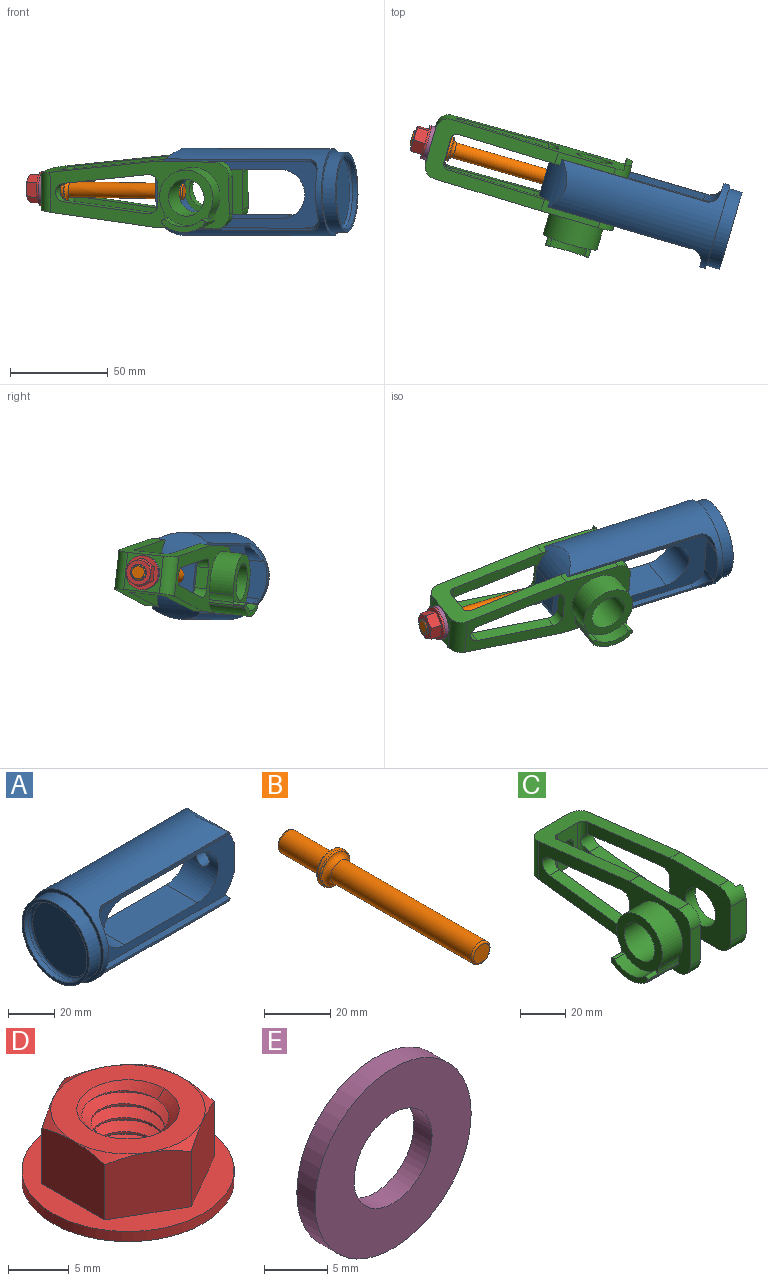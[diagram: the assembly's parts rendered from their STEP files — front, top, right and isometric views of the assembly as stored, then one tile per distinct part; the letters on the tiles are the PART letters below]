
ASSEMBLY  parts=5 mates=5
PART A: 35 faces, bbox 99.1x44.5x44.5 mm
  f0: cylinder r=22.23mm len=85.62mm, axis (-1,0,0), area 4765.1mm2, adj f4,f5,f8,f9,f12,f13,f22,f25
  f1: plane 88.9x34.29mm, normal (0,1,0), area 1346.2mm2, adj f3,f6,f7,f12,f14,f15,f16,f17
  f2: plane 88.9x34.29mm, normal (0,-1,0), area 1346.2mm2, adj f3,f10,f11,f13,f14,f15,f16,f17
  f3: plane 19.05x15.86mm, normal (1,0,0), area 252.7mm2, adj f1,f2,f24,f25,f26
  f4: plane 77.16x1.2mm, normal (0,1,0), area 83.9mm2, adj f0,f6,f19,f25,f29
  f5: plane 77.16x1.2mm, normal (0,1,0), area 83.9mm2, adj f0,f7,f20,f26,f30
  f6: plane 75.89x3.18mm, normal (0,0,-1), area 241mm2, adj f1,f4,f19,f25
  f7: plane 75.89x3.18mm, normal (0,0,1), area 241mm2, adj f1,f5,f20,f26
  f8: plane 77.16x1.2mm, normal (0,-1,0), area 83.9mm2, adj f0,f11,f18,f25,f27
  f9: plane 77.16x1.2mm, normal (0,-1,0), area 83.9mm2, adj f0,f10,f21,f26,f28
  f10: plane 75.89x3.18mm, normal (0,0,1), area 241mm2, adj f2,f9,f21,f26
  f11: plane 75.89x3.18mm, normal (0,0,-1), area 241mm2, adj f2,f8,f18,f25
  f12: plane 22.9x12.7mm, normal (1,0,0), area 230.7mm2, adj f0,f1,f19,f20,f29,f30
  f13: plane 22.9x12.7mm, normal (1,0,0), area 230.7mm2, adj f0,f2,f18,f21,f27,f28
  f14: plane 44.45x19.05mm, normal (0,0,-1), area 846.8mm2, adj f1,f2,f15,f17
  f15: cylinder r=12.7mm len=25.4mm, axis (0,-1,0), area 760.1mm2, adj f1,f2,f14,f16
  f16: plane 44.45x19.05mm, normal (0,0,1), area 846.8mm2, adj f1,f2,f15,f17
  f17: cylinder r=12.7mm len=25.4mm, axis (0,-1,0), area 709.9mm2, adj f1,f2,f14,f16,f24
  f18: cylinder r=7.62mm len=9.53mm, axis (0,-1,0), area 63.1mm2, adj f2,f8,f11,f13,f27
  f19: cylinder r=7.62mm len=9.53mm, axis (0,-1,0), area 63.1mm2, adj f1,f4,f6,f12,f29
  f20: cylinder r=7.62mm len=9.53mm, axis (0,1,0), area 63.1mm2, adj f1,f5,f7,f12,f30
  f21: cylinder r=7.62mm len=9.53mm, axis (0,1,0), area 63.1mm2, adj f2,f9,f10,f13,f28
  f22: plane 44.45x44.45mm, normal (-1,0,0), area 230.2mm2, adj f0,f23
  f23: cylinder r=20.51mm len=41.02mm, axis (-1,0,0), area 900.2mm2, adj f22,f32
  f24: cylinder r=3.97mm len=10.16mm, axis (1,0,0), area 245.4mm2, adj f3,f17
  f25: cylinder r=25.4mm len=25.4mm, axis (0,-1,0), area 355.4mm2, adj f0,f1,f2,f3,f4,f6,f8,f11
  f26: cylinder r=25.4mm len=25.4mm, axis (0,-1,0), area 355.4mm2, adj f0,f1,f2,f3,f5,f7,f9,f10
  f27: cylinder r=6.35mm len=8.71mm, axis (0,0,1), area 20.6mm2, adj f0,f8,f13,f18
  f28: cylinder r=6.35mm len=8.71mm, axis (0,0,1), area 20.6mm2, adj f0,f9,f13,f21
  f29: cylinder r=6.35mm len=8.71mm, axis (0,0,-1), area 20.6mm2, adj f0,f4,f12,f19
  f30: cylinder r=6.35mm len=8.71mm, axis (0,0,-1), area 20.6mm2, adj f0,f5,f12,f20
  f31: cylinder r=19.05mm len=38.1mm, axis (1,0,0), area 304mm2, adj f32,f34
  f32: plane 41.02x41.02mm, normal (-1,0,0), area 181.5mm2, adj f23,f31
  f33: plane 35.56x35.56mm, normal (-1,0,0), area 993.1mm2, adj f34
  f34: torus R=17.78mm, axis (1,0,0), area 233mm2, adj f31,f33
PART B: 13 faces, bbox 15.6x83.2x15.6 mm
  f0: plane 6.67x6.67mm, normal (0,-1,0), area 34.9mm2, adj f12
  f1: plane 6.67x6.67mm, normal (0,1,0), area 34.9mm2, adj f2
  f2: torus R=3.33mm, axis (0,-1,0), area 23.4mm2, adj f1,f3
  f3: cylinder r=3.97mm len=18.03mm, axis (0,-1,0), area 449.7mm2, adj f2,f4
  f4: torus R=4.35mm, axis (0,-1,0), area 15.4mm2, adj f3,f5
  f5: plane 11.94x11.94mm, normal (0,1,0), area 52.5mm2, adj f4,f6
  f6: torus R=5.97mm, axis (0,-1,0), area 23.4mm2, adj f5,f7
  f7: cylinder r=6.35mm len=12.7mm, axis (0,-1,0), area 45.6mm2, adj f6,f8
  f8: torus R=5.97mm, axis (0,-1,0), area 23.4mm2, adj f7,f9
  f9: plane 11.94x11.94mm, normal (0,-1,0), area 3.5mm2, adj f8,f10
  f10: torus R=5.87mm, axis (0,-1,0), area 87.6mm2, adj f9,f11
  f11: cylinder r=3.97mm len=59.69mm, axis (0,-1,0), area 1488.5mm2, adj f10,f12
  f12: torus R=3.33mm, axis (0,-1,0), area 23.4mm2, adj f0,f11
PART C: 52 faces, bbox 54x101.6x34.3 mm
  f0: cylinder r=14.29mm len=28.58mm, axis (1,0,0), area 757.5mm2, adj f2,f38,f48,f49
  f1: plane 92.08x34.29mm, normal (1,0,0), area 1682.2mm2, adj f5,f6,f7,f8,f9,f20,f21,f24
  f2: plane 95.25x34.29mm, normal (-1,0,0), area 1339.9mm2, adj f0,f3,f6,f8,f10,f11,f18,f19
  f3: plane 30.48x6.35mm, normal (0,0,1), area 193.5mm2, adj f2,f8,f16,f18
  f4: plane 19.05x9.53mm, normal (0,-1,0), area 181.5mm2, adj f14,f20,f21,f37
  f5: plane 30.48x6.35mm, normal (0,0,-1), area 193.5mm2, adj f1,f6,f14,f21
  f6: plane 63.5x31.75mm, normal (0,0.12,-0.99), area 969.7mm2, adj f1,f2,f5,f11,f12,f14,f15,f16
  f7: cylinder r=9.53mm len=19.05mm, axis (-1,0,0), area 380mm2, adj f1,f14
  f8: plane 63.5x31.75mm, normal (0,0.12,0.99), area 969.7mm2, adj f1,f2,f3,f9,f12,f14,f15,f16
  f9: plane 30.48x6.35mm, normal (0,0,1), area 193.5mm2, adj f1,f8,f14,f20
  f10: plane 19.05x6.35mm, normal (0,-1,0), area 121mm2, adj f2,f16,f18,f19
  f11: plane 30.48x6.35mm, normal (0,0,-1), area 193.5mm2, adj f2,f6,f16,f19
  f12: plane 19.05x19.05mm, normal (0,1,0), area 313.4mm2, adj f6,f8,f17,f50,f51
  f13: cylinder r=9.53mm len=19.05mm, axis (-1,0,0), area 1140.1mm2, adj f16,f38
  f14: plane 89.54x34.29mm, normal (-1,0,0), area 1667.4mm2, adj f4,f5,f6,f7,f8,f9,f20,f21
  f15: plane 21.18x12.7mm, normal (0,-1,0), area 219.5mm2, adj f6,f8,f17,f22,f23
  f16: plane 89.54x34.29mm, normal (1,0,0), area 1667.4mm2, adj f3,f6,f8,f10,f11,f13,f18,f19
  f17: cylinder r=3.97mm len=8.89mm, axis (0,1,0), area 221.7mm2, adj f12,f15
  f18: cylinder r=7.62mm len=7.62mm, axis (-1,0,0), area 76mm2, adj f2,f3,f10,f16
  f19: cylinder r=7.62mm len=7.62mm, axis (1,0,0), area 76mm2, adj f2,f10,f11,f16
  f20: cylinder r=7.62mm len=9.53mm, axis (-1,0,0), area 98.9mm2, adj f1,f4,f9,f14,f36,f37
  f21: cylinder r=7.62mm len=9.53mm, axis (1,0,0), area 98.9mm2, adj f1,f4,f5,f14,f36,f37
  f22: cylinder r=3.17mm len=21.95mm, axis (0,0,-1), area 85.2mm2, adj f6,f8,f15,f16,f35
  f23: cylinder r=3.17mm len=21.95mm, axis (0,0,1), area 85.2mm2, adj f6,f8,f14,f15,f24
  f24: cylinder r=4.76mm len=9.46mm, axis (1,0,0), area 97.8mm2, adj f1,f14,f23,f25,f29
  f25: plane 44.84x6.35mm, normal (0,-0.12,0.99), area 286.8mm2, adj f1,f14,f24,f26
  f26: cylinder r=4.76mm len=6.35mm, axis (1,0,0), area 51.1mm2, adj f1,f14,f25,f27
  f27: plane 10.76x6.35mm, normal (0,1,0), area 68.3mm2, adj f1,f14,f26,f28
  f28: cylinder r=4.76mm len=6.35mm, axis (1,0,0), area 51.1mm2, adj f1,f14,f27,f29
  f29: plane 44.84x6.35mm, normal (0,-0.12,-0.99), area 286.8mm2, adj f1,f14,f24,f28
  f30: plane 44.84x6.35mm, normal (0,-0.12,-0.99), area 286.8mm2, adj f2,f16,f31,f35
  f31: cylinder r=4.76mm len=6.35mm, axis (1,0,0), area 51.1mm2, adj f2,f16,f30,f32
  f32: plane 10.76x6.35mm, normal (0,1,0), area 68.3mm2, adj f2,f16,f31,f33
  f33: cylinder r=4.76mm len=6.35mm, axis (1,0,0), area 51.1mm2, adj f2,f16,f32,f34
  f34: plane 44.84x6.35mm, normal (0,-0.12,0.99), area 286.8mm2, adj f2,f16,f33,f35
  f35: cylinder r=4.76mm len=9.46mm, axis (1,0,0), area 97.8mm2, adj f2,f16,f22,f30,f34
  f36: plane 31.43x3.18mm, normal (0,1,0), area 99.8mm2, adj f1,f20,f21,f37
  f37: plane 31.43x3.18mm, normal (1,0,0), area 88mm2, adj f4,f20,f21,f36
  f38: plane 28.58x28.58mm, normal (-1,0,0), area 361.1mm2, adj f0,f13,f39,f43,f44,f46,f47,f48
  f39: cylinder r=14.29mm len=18.66mm, axis (1,0,0), area 129.1mm2, adj f38,f45,f46,f47
  f40: cylinder r=1.27mm len=19.05mm, axis (1,0,0), area 21.2mm2, adj f2,f41,f44,f45
  f41: cylinder r=17.14mm len=21.95mm, axis (1,0,0), area 453.7mm2, adj f2,f40,f42,f45
  f42: cylinder r=1.27mm len=19.05mm, axis (1,0,0), area 21.2mm2, adj f2,f41,f43,f45
  f43: plane 19.05x1.38mm, normal (0,-1,0), area 20.2mm2, adj f2,f38,f42,f45,f47,f49
  f44: plane 19.05x1.38mm, normal (0,1,0), area 20.2mm2, adj f2,f38,f40,f45,f46,f48
  f45: plane 22.86x6.63mm, normal (-1,0,0), area 69.3mm2, adj f39,f40,f41,f42,f43,f44,f46,f47
  f46: cylinder r=1.27mm len=6.35mm, axis (1,0,0), area 18.4mm2, adj f38,f39,f44,f45
  f47: cylinder r=1.27mm len=6.35mm, axis (1,0,0), area 18.4mm2, adj f38,f39,f43,f45
  f48: cylinder r=7.62mm len=12.7mm, axis (1,0,0), area 50mm2, adj f0,f2,f38,f44
  f49: cylinder r=7.62mm len=12.7mm, axis (1,0,0), area 50mm2, adj f0,f2,f38,f43
  f50: cylinder r=6.35mm len=20.57mm, axis (0,0,1), area 195.5mm2, adj f2,f6,f8,f12
  f51: cylinder r=6.35mm len=20.57mm, axis (0,0,-1), area 195.5mm2, adj f1,f6,f8,f12
PART D: 43 faces, bbox 18.1x18.1x8.3 mm
  f0: cone r=0mm half-angle=60deg, axis (0,0,-1), area 4mm2, adj f9,f10,f12
  f1: cone r=0mm half-angle=60deg, axis (0,0,-1), area 4mm2, adj f10,f11,f12
  f2: cone r=0mm half-angle=60deg, axis (0,0,-1), area 4mm2, adj f6,f11,f12
  f3: cone r=0mm half-angle=60deg, axis (0,0,-1), area 4mm2, adj f6,f7,f12
  f4: cone r=0mm half-angle=60deg, axis (0,0,-1), area 4mm2, adj f7,f8,f12
  f5: cone r=0mm half-angle=60deg, axis (0,0,-1), area 4mm2, adj f8,f9,f12
  f6: plane 6.95x6.73mm, normal (-0.5,0.87,0), area 43.5mm2, adj f2,f3,f7,f11,f13
  f7: plane 7.93x6.73mm, normal (-1,0,0), area 43.5mm2, adj f3,f4,f6,f8,f13
  f8: plane 6.95x6.73mm, normal (-0.5,-0.87,0), area 43.5mm2, adj f4,f5,f7,f9,f13
  f9: plane 6.95x6.73mm, normal (0.5,-0.87,0), area 43.5mm2, adj f0,f5,f8,f10,f13
  f10: plane 7.93x6.73mm, normal (1,0,0), area 43.5mm2, adj f0,f1,f9,f11,f13
  f11: plane 6.95x6.73mm, normal (0.5,0.87,0), area 43.5mm2, adj f1,f2,f6,f10,f13
  f12: plane 12.7x12.7mm, normal (0,0,1), area 70.8mm2, adj f0,f1,f2,f3,f4,f5,f15,f16
  f13: plane 17.46x17.46mm, normal (0,0,1), area 99.8mm2, adj f6,f7,f8,f9,f10,f11,f35
  f14: cone r=0mm half-angle=45deg, axis (0,0,1), area 0.3mm2, adj f16,f18,f36
  f15: cone r=0mm half-angle=45deg, axis (0,0,1), area 9.4mm2, adj f12,f16,f38
  f16: cone r=0mm half-angle=45deg, axis (0,0,1), area 14.2mm2, adj f12,f14,f15,f17,f34,f36,f38
  f17: cylinder r=3.05mm len=0.83mm, axis (0,0,1), area 0mm2, adj f16,f18,f38
  f18: cylinder r=3.05mm len=6.09mm, axis (0,0,1), area 1.6mm2, adj f14,f17,f19,f36,f38
  f19: cylinder r=3.05mm len=6.09mm, axis (0,0,1), area 1.7mm2, adj f18,f20,f36,f38
  f20: cylinder r=3.05mm len=6.09mm, axis (0,0,1), area 1.7mm2, adj f19,f21,f36,f38
  f21: cylinder r=3.05mm len=6.09mm, axis (0,0,1), area 1.7mm2, adj f20,f22,f36,f38
  f22: cylinder r=3.05mm len=6.09mm, axis (0,0,1), area 1.7mm2, adj f21,f23,f36,f38
  f23: cylinder r=3.05mm len=6.09mm, axis (0,0,1), area 1.7mm2, adj f22,f24,f36,f38
  f24: cylinder r=3.05mm len=6.08mm, axis (0,0,1), area 1.4mm2, adj f23,f36,f37,f38
  f25: cylinder r=3.96mm len=7.92mm, axis (0,0,-1), area 2.2mm2, adj f26,f36,f38,f39
  f26: cylinder r=3.96mm len=7.92mm, axis (0,0,-1), area 2.2mm2, adj f25,f27,f36,f38
  f27: cylinder r=3.96mm len=7.92mm, axis (0,0,-1), area 2.2mm2, adj f26,f28,f36,f38
  f28: cylinder r=3.96mm len=7.92mm, axis (0,0,-1), area 2.2mm2, adj f27,f29,f36,f38
  f29: cylinder r=3.96mm len=7.92mm, axis (0,0,-1), area 2.2mm2, adj f28,f30,f36,f38
  f30: cylinder r=3.96mm len=7.92mm, axis (0,0,-1), area 2.2mm2, adj f29,f31,f36,f38
  f31: cylinder r=3.96mm len=7.92mm, axis (0,0,-1), area 2.2mm2, adj f30,f32,f36,f38
  f32: cylinder r=3.96mm len=7.92mm, axis (0,0,-1), area 2.2mm2, adj f31,f33,f36,f38
  f33: cylinder r=3.96mm len=7.92mm, axis (0,0,-1), area 2.2mm2, adj f32,f34,f36,f38
  f34: cylinder r=3.96mm len=3.72mm, axis (0,0,-1), area 0.6mm2, adj f16,f33,f36,f38
  f35: cylinder r=8.73mm len=17.46mm, axis (0,0,-1), area 55.7mm2, adj f13,f40
  f36: bspline ~9.15x7.92mm, area 95.1mm2, adj f14,f16,f18,f19,f20,f21,f22,f23
  f37: cone r=0mm half-angle=45deg, axis (0,0,-1), area 1mm2, adj f24,f36,f38,f42
  f38: bspline ~7.92x7.92mm, area 95.2mm2, adj f15,f16,f17,f18,f19,f20,f21,f22
  f39: cylinder r=3.96mm len=2.95mm, axis (0,0,-1), area 0.3mm2, adj f25,f36,f38,f42
  f40: plane 17.46x17.46mm, normal (0,0,-1), area 183.6mm2, adj f35,f41,f42
  f41: cone r=0mm half-angle=45deg, axis (0,0,-1), area 8.5mm2, adj f36,f40,f42
  f42: cone r=0mm half-angle=45deg, axis (0,0,-1), area 14.5mm2, adj f36,f37,f38,f39,f40,f41
PART E: 4 faces, bbox 17.5x2x17.5 mm
  f0: cylinder r=8.74mm len=17.48mm, axis (0,-1,0), area 111.6mm2, adj f1,f2
  f1: plane 17.48x17.48mm, normal (0,-1,0), area 179.9mm2, adj f0,f3
  f2: plane 17.48x17.48mm, normal (0,1,0), area 179.9mm2, adj f0,f3
  f3: cylinder r=4.37mm len=8.74mm, axis (0,1,0), area 55.8mm2, adj f1,f2
PLACE A rot(axis=(-0.01,-0.05,1),163.7deg) t=(-56.93,-115.42,-73.82)mm
PLACE B rot(axis=(-0.49,0.67,0.56),107.6deg) t=(-153.4,-87.3,-73.12)mm
PLACE C rot(axis=(0.07,-0.06,1),74deg) t=(-127.44,-94.84,-73.63)mm
PLACE D rot(axis=(-0.67,-0.56,0.49),107.3deg) t=(-215.52,-69.28,-71.89)mm
PLACE E rot(axis=(-0.6,0.8,0.04),175.8deg) t=(-206.71,-71.84,-72.07)mm
MATE pin_slot C.f7 <-> A.f15  axis (-0.28,-0.95,-0.11) through (-124.78,-85.74,-72.62)mm
MATE fastened B.f2 <-> C.f17  axis (-0.96,0.28,0.02) through (-198.17,-74.32,-72.23)mm
MATE fastened D.f0 <-> E.f0  axis (0.96,-0.28,-0.02) through (-208.66,-71.27,-72.03)mm
MATE fastened E.f0 <-> C.f17  axis (0.96,-0.28,-0.02) through (-206.71,-71.84,-72.07)mm
MATE slider C.f17 <-> B.f2  axis (-0.96,0.28,0.02) through (-198.17,-74.32,-72.23)mm
